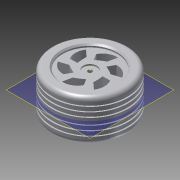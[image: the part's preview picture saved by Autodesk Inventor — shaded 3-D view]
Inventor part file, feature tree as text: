
AUTODESK INVENTOR PART (.ipt)
format: ipt  version: 2015 (Build 190159000, 159)  size: 282,624 bytes
history: native  units: mm
features: sketch x8, extrude x3, revolve x2, fillet x2, hole x2, chamfer x1, pattern_circular x1, plane x1, mirror x1, projected_geometry x1
ambient origin geometry x8: Origin, YZ Plane, XZ Plane, XY Plane, X Axis, Y Axis, Z Axis, Center Point
bodies: Solid1 (feature_tree)
feature tree (22):
  revolve  "Revolution1"  [1 undecoded]
  extrude  "Extrusion4"  TaperAngle=90.0deg  [1 undecoded]
  fillet  "Fillet4"  Radius=48.0mm
  sketch  "Sketch8"  dims[d36=3.0mm d37=3.0mm d38=2.0mm d39=0.0mm]
  fillet  "Fillet5"  Radius=13.0mm
  extrude  "Extrusion5"  Depth=3.0mm
  chamfer  "Chamfer1"  Distance=2.0mm
  extrude  "Extrusion6"  Depth=2.0mm TaperAngle=0.0deg
  pattern_circular  "Circular Pattern2"  Count=6 Angle=360.0deg
  sketch  "Sketch11"  dims[d55=3.2mm d56=6.0mm d57=10.0mm d58=2.0mm d59=90.0deg d60=8.0mm d61=20.594885mm d62=1.0mm]
  hole  "Hole3"  [1 undecoded]
  hole  "Hole4"  [1 undecoded]
  revolve  "Revolution2"  [1 undecoded]
  plane  "Work Plane1"
  mirror  "Mirror1"
  sketch  "Sketch1"  dims[d2=5.0mm d3=30.0mm]
  sketch  "Sketch7"  dims[d4=23.0mm d5=90.0deg d33=48.0mm d34=13.0mm d35=0.0mm]
  projected_geometry  "Projected Loop1"
  sketch  "Sketch9"  dims[d40=1.0mm d41=2.0mm d42=45.0deg d43=2.0mm d44=0.0mm d45=60.0mm d46=360.0deg]
  sketch  "Sketch10"  dims[d48=3.2mm d49=6.0mm d50=10.0mm d51=3.0mm d52=90.0deg d53=8.0mm d54=20.594885mm]
  sketch  "Sketch12"  dims[d63=1.0mm d64=1.0mm d65=1.0mm]
  sketch  "Sketch13"  dims[d66=1.0mm d67=1.0mm d68=10.0mm d69=2.5mm d70=2.5mm d71=90.0deg]
note: 5 required parameter values undecoded (feature->parameter linkage not recoverable at this tier; creation-order binding heuristic only, values carry confidence <= 0.55)